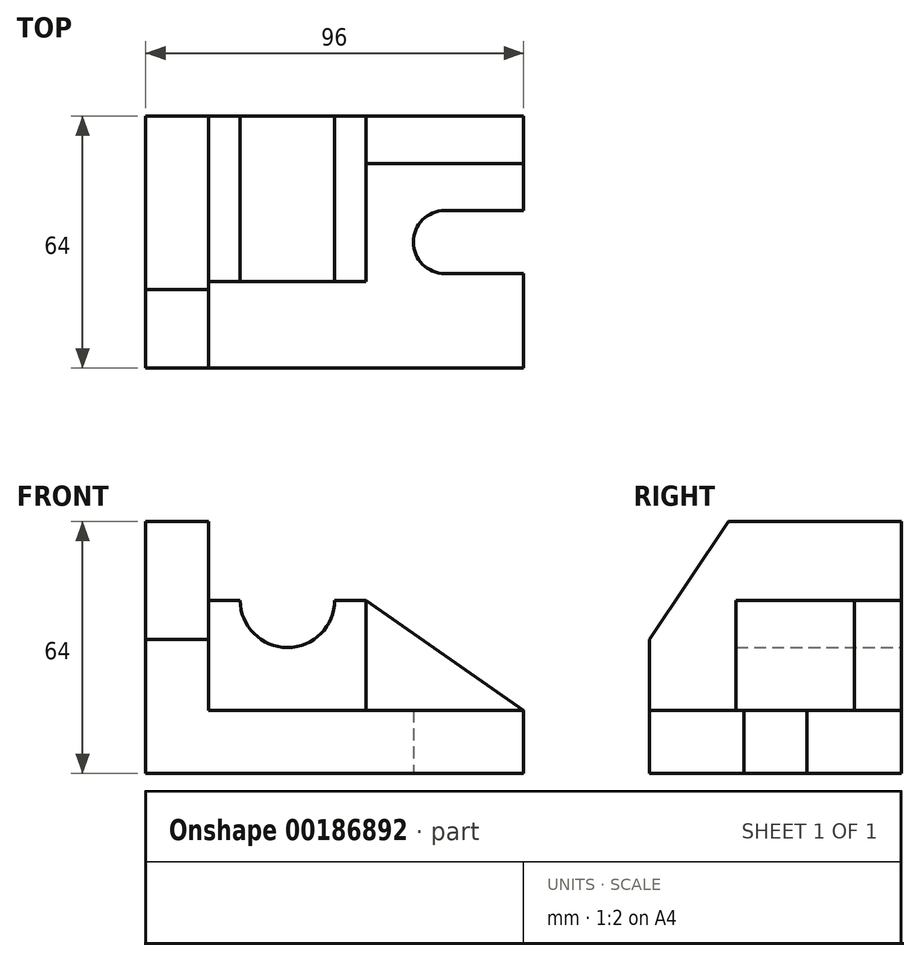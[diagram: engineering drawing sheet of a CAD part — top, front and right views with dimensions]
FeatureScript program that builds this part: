
annotation { "Feature Type Name" : "Feature", "Feature Type Description" : "" }
export const myFeature = defineFeature(function(context is Context, id is Id, definition is map)
    precondition{}
    {
        {
            var Q0;
            Q0=qCreatedBy(makeId("Top.planeOp"),FACE);
            var sketch = newSketch(context, id + "F0", { "sketchPlane" : qUnion([Q0])});
            skLineSegment(sketch, "E0.bottom", {"start": v(-48, -32) * mm, "end": v(48, -32) * mm});
            skLineSegment(sketch, "E0.top", {"start": v(-48, 32) * mm, "end": v(48, 32) * mm});
            skLineSegment(sketch, "E0.left", {"start": v(-48, -32) * mm, "end": v(-48, 32) * mm});
            skLineSegment(sketch, "E0.right", {"start": v(48, -32) * mm, "end": v(48, -8) * mm});
            skPoint(sketch, "E0.middle", {"position": v(0, 0) * mm});
            skArc(sketch, "E1", {"start": v(28, 8) * mm, "mid": v(20, 0) * mm, "end": v(28, -8) * mm});
            skLineSegment(sketch, "E2", {"start": v(28, -8) * mm, "end": v(48, -8) * mm});
            skLineSegment(sketch, "E3", {"start": v(28, 8) * mm, "end": v(48, 8) * mm});
            skLineSegment(sketch, "E4.trimOffspring", {"start": v(48, 8) * mm, "end": v(48, 32) * mm});
            skSolve(sketch);
        }
        {
            var Q0;
            Q0=makeQuery(id+"F0.imprint","IMPRINT",FACE,{"disambiguationData":[TD([[makeQuery(id+"F0.imprint","IMPRINT",EDGE,{"derivedFrom":sQuery(id+"F0.wireOp",EDGE,"E0.bottom")}),1.0]])]});
            extrude(context, id + "F1", {"entities" : qUnion([Q0]), "depth" : 16 * mm});
        }
        {
            var Q0;
            Q0=makeQuery(id+"F1.opExtrude","SWEPT_FACE",FACE,{"disambiguationData":[OSD([sQuery(id+"F0.wireOp",EDGE,"E0.left")])]});
            var sketch = newSketch(context, id + "F2", { "sketchPlane" : qUnion([Q0])});
            skLineSegment(sketch, "E5", {"start": v(-32, 0) * mm, "end": v(-32, 64) * mm});
            skLineSegment(sketch, "E6", {"start": v(-32, 64) * mm, "end": v(12, 64) * mm});
            skLineSegment(sketch, "E7", {"start": v(12, 64) * mm, "end": v(32, 34) * mm});
            skLineSegment(sketch, "E8", {"start": v(32, 34) * mm, "end": v(32, 0) * mm});
            skLineSegment(sketch, "E9", {"start": v(32, 0) * mm, "end": v(-32, 0) * mm});
            skSolve(sketch);
        }
        {
            var Q0;
            {var subQ3=sQuery(id+"F2.wireOp",EDGE,"E6");Q0=makeQuery(id+"F2.imprint","IMPRINT",FACE,{"disambiguationData":[TD([[makeQuery(id+"F2.imprint","IMPRINT",EDGE,{"derivedFrom":subQ3}),-1.0]])]});}
            extrude(context, id + "F3", {"entities" : qUnion([Q0]), "operationType" : NewBodyOperationType.ADD, "oppositeDirection" : true, "depth" : 16 * mm});
        }
        {
            var Q0;
            Q0=makeQuery(id+"F3.boolean.opBoolean","MERGE",FACE,{"derivedFrom":[makeQuery(id+"F1.opExtrude","SWEPT_FACE",FACE,{"disambiguationData":[OSD([sQuery(id+"F0.wireOp",EDGE,"E0.top")])]}),makeQuery(id+"F3.opExtrude","SWEPT_FACE",FACE,{"disambiguationData":[OSD([sQuery(id+"F2.wireOp",EDGE,"E5")])]})]});
            var sketch = newSketch(context, id + "F4", { "sketchPlane" : qUnion([Q0])});
            skLineSegment(sketch, "E10", {"start": v(32, 16) * mm, "end": v(-8, 16) * mm});
            skLineSegment(sketch, "E11", {"start": v(-8, 16) * mm, "end": v(-8, 44) * mm});
            skLineSegment(sketch, "E12", {"start": v(-8, 44) * mm, "end": v(0, 44) * mm});
            skLineSegment(sketch, "E13", {"start": v(32, 44) * mm, "end": v(32, 16) * mm});
            skArc(sketch, "E14", {"start": v(0, 44) * mm, "mid": v(12, 32) * mm, "end": v(24, 44) * mm});
            skLineSegment(sketch, "E15.trimOffspring", {"start": v(24, 44) * mm, "end": v(32, 44) * mm});
            skSolve(sketch);
        }
        {
            var Q0;
            Q0=makeQuery(id+"F4.imprint","IMPRINT",FACE,{"disambiguationData":[TD([[makeQuery(id+"F4.imprint","IMPRINT",EDGE,{"derivedFrom":sQuery(id+"F4.wireOp",EDGE,"E10")}),-1.0]])]});
            extrude(context, id + "F5", {"entities" : qUnion([Q0]), "operationType" : NewBodyOperationType.ADD, "oppositeDirection" : true, "depth" : 42 * mm});
        }
        {
            var Q0;
            Q0=makeQuery(id+"F5.boolean.opBoolean","MERGE",FACE,{"derivedFrom":[makeQuery(id+"F3.boolean.opBoolean","MERGE",FACE,{"derivedFrom":[makeQuery(id+"F1.opExtrude","SWEPT_FACE",FACE,{"disambiguationData":[OSD([sQuery(id+"F0.wireOp",EDGE,"E0.top")])]}),makeQuery(id+"F3.opExtrude","SWEPT_FACE",FACE,{"disambiguationData":[OSD([sQuery(id+"F2.wireOp",EDGE,"E5")])]})]}),makeQuery(id+"F5.opExtrude","CAP_FACE",FACE,{"disambiguationData":[OSD([sQuery(id+"F4.wireOp",EDGE,"E10"),sQuery(id+"F4.wireOp",EDGE,"E11"),sQuery(id+"F4.wireOp",EDGE,"E12"),sQuery(id+"F4.wireOp",EDGE,"E13"),sQuery(id+"F4.wireOp",EDGE,"E14"),sQuery(id+"F4.wireOp",EDGE,"E15.trimOffspring")])],"isStart":true})]});
            var sketch = newSketch(context, id + "F6", { "sketchPlane" : qUnion([Q0])});
            skLineSegment(sketch, "E16", {"start": v(-48, 16) * mm, "end": v(-8, 16) * mm});
            skLineSegment(sketch, "E17", {"start": v(-8, 16) * mm, "end": v(-8, 44) * mm});
            skLineSegment(sketch, "E18", {"start": v(-8, 44) * mm, "end": v(-48, 16) * mm});
            skSolve(sketch);
        }
        {
            var Q0;
            Q0=makeQuery(id+"F6.imprint","IMPRINT",FACE,{"disambiguationData":[TD([[makeQuery(id+"F6.imprint","IMPRINT",EDGE,{"derivedFrom":sQuery(id+"F6.wireOp",EDGE,"E16")}),-1.0]])]});
            extrude(context, id + "F7", {"entities" : qUnion([Q0]), "operationType" : NewBodyOperationType.ADD, "oppositeDirection" : true, "depth" : 12 * mm});
        }
    });
